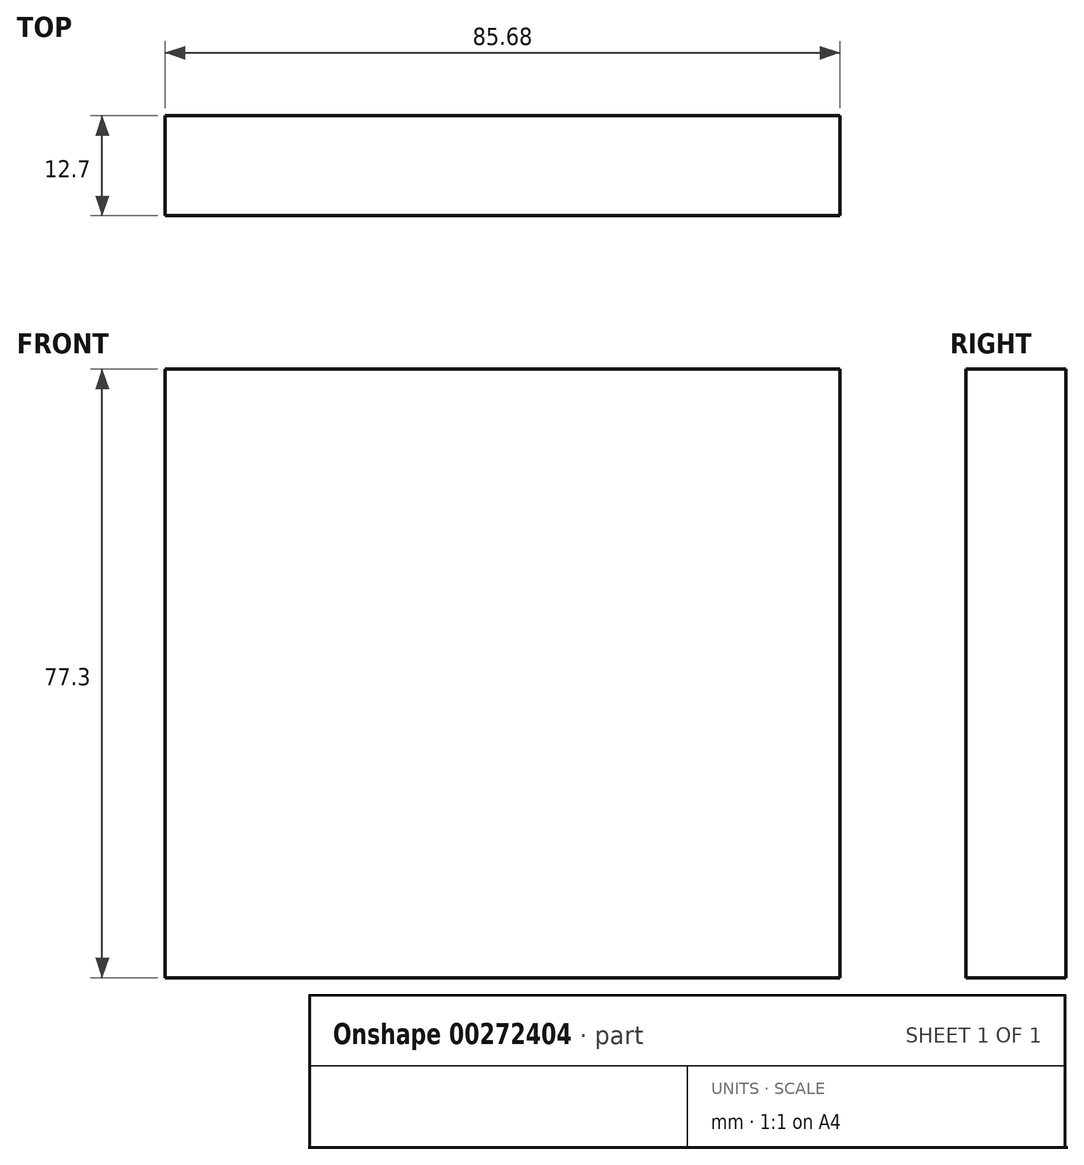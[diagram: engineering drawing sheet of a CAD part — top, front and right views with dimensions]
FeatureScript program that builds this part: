
annotation { "Feature Type Name" : "Feature", "Feature Type Description" : "" }
export const myFeature = defineFeature(function(context is Context, id is Id, definition is map)
    precondition{}
    {
        {
            var Q0;
            Q0=qCreatedBy(makeId("Front.planeOp"),FACE);
            var sketch = newSketch(context, id + "F0", { "sketchPlane" : qUnion([Q0])});
            skLineSegment(sketch, "E0.bottom", {"start": v(-41.24, 37.91) * mm, "end": v(44.44, 37.91) * mm});
            skLineSegment(sketch, "E0.top", {"start": v(-41.24, -39.39) * mm, "end": v(44.44, -39.39) * mm});
            skLineSegment(sketch, "E0.left", {"start": v(-41.24, 37.91) * mm, "end": v(-41.24, -39.39) * mm});
            skLineSegment(sketch, "E0.right", {"start": v(44.44, 37.91) * mm, "end": v(44.44, -39.39) * mm});
            skSolve(sketch);
        }
        {
            var Q0;
            Q0 = qSketchRegion(id + "F0", true);
            extrude(context, id + "F1", {"entities" : qUnion([Q0]), "depth" : 12.7 * mm});
        }
    });
